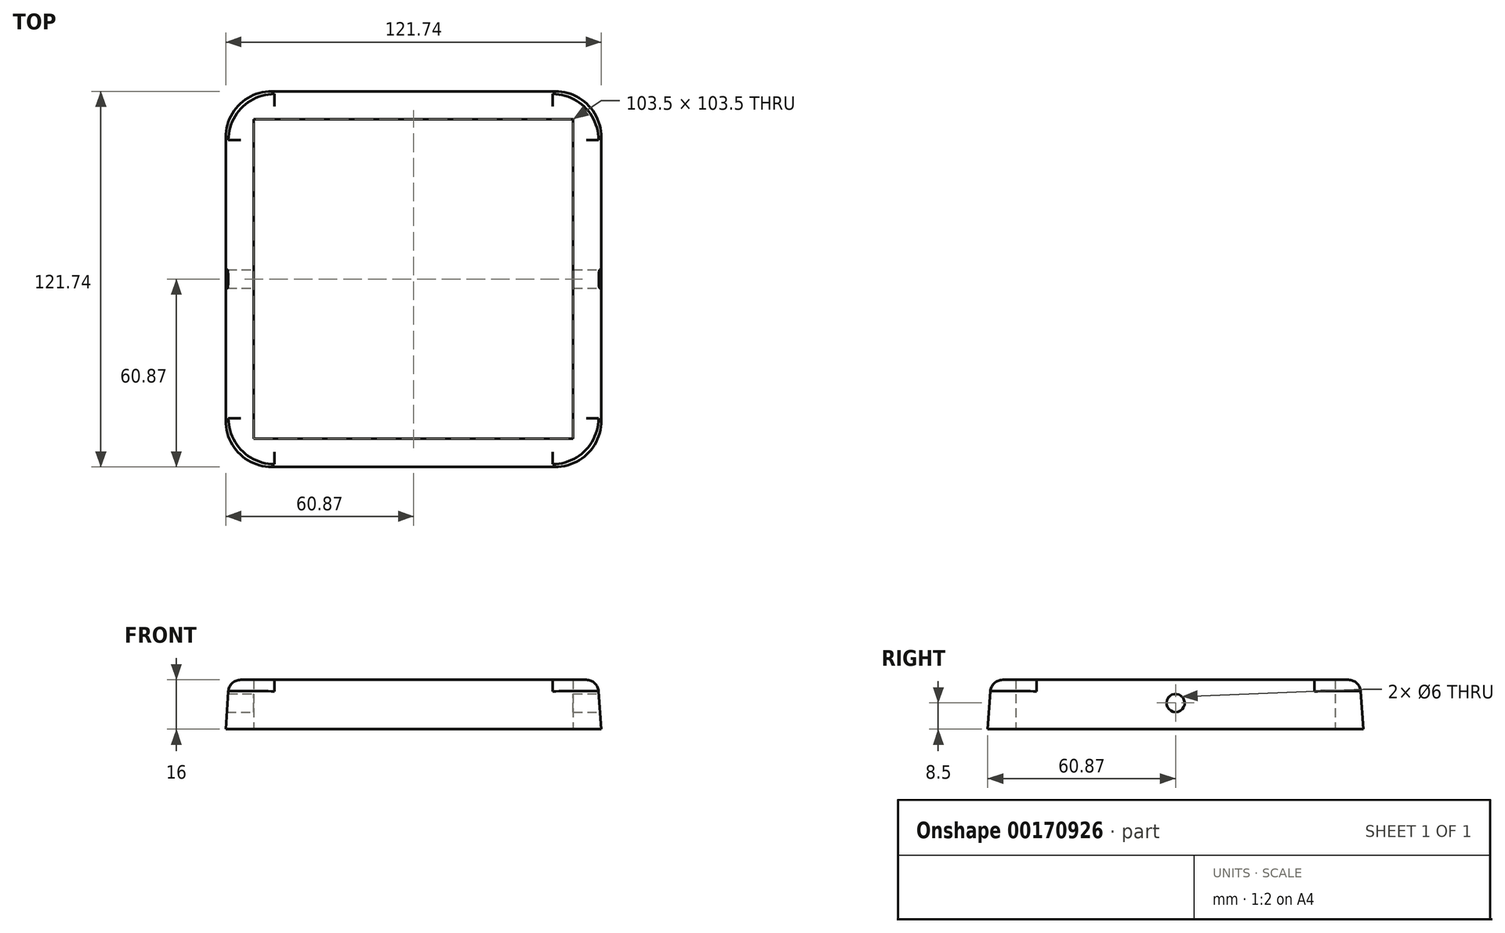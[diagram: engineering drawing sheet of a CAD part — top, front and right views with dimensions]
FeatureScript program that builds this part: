
annotation { "Feature Type Name" : "Feature", "Feature Type Description" : "" }
export const myFeature = defineFeature(function(context is Context, id is Id, definition is map)
    precondition{}
    {
        {
            var Q0;
            Q0=qCreatedBy(makeId("Top.planeOp"),FACE);
            var sketch = newSketch(context, id + "F0", { "sketchPlane" : qUnion([Q0])});
            skLineSegment(sketch, "E0.bottom", {"start": v(51.25, 51.25) * mm, "end": v(-51.25, 51.25) * mm});
            skLineSegment(sketch, "E0.top", {"start": v(51.25, -51.25) * mm, "end": v(-51.25, -51.25) * mm});
            skLineSegment(sketch, "E0.left", {"start": v(51.25, 51.25) * mm, "end": v(51.25, -51.25) * mm});
            skLineSegment(sketch, "E0.right", {"start": v(-51.25, 51.25) * mm, "end": v(-51.25, -51.25) * mm});
            skPoint(sketch, "E0.middle", {"position": v(0, 0) * mm});
            skSolve(sketch);
        }
        {
            var Q0;
            Q0=makeQuery(id+"F0.imprint","IMPRINT",FACE,{"disambiguationData":[TD([[makeQuery(id+"F0.imprint","IMPRINT",EDGE,{"derivedFrom":sQuery(id+"F0.wireOp",EDGE,"E0.bottom")}),1.0]])]});
            extrude(context, id + "F1", {"entities" : qUnion([Q0]), "depth" : 100 * mm});
        }
        {
            var Q0;
            Q0=makeQuery(id+"F1.opExtrude","CAP_FACE",FACE,{"disambiguationData":[OSD([sQuery(id+"F0.wireOp",EDGE,"E0.bottom"),sQuery(id+"F0.wireOp",EDGE,"E0.top"),sQuery(id+"F0.wireOp",EDGE,"E0.left"),sQuery(id+"F0.wireOp",EDGE,"E0.right")])],"isStart":false});
            var sketch = newSketch(context, id + "F2", { "sketchPlane" : qUnion([Q0])});
            skLineSegment(sketch, "E1.0", {"start": v(51.75, -51.75) * mm, "end": v(-51.75, -51.75) * mm});
            skLineSegment(sketch, "E1.1", {"start": v(51.75, 51.75) * mm, "end": v(51.75, -51.75) * mm});
            skLineSegment(sketch, "E1.2", {"start": v(51.75, 51.75) * mm, "end": v(-51.75, 51.75) * mm});
            skLineSegment(sketch, "E1.3", {"start": v(-51.75, 51.75) * mm, "end": v(-51.75, -51.75) * mm});
            skLineSegment(sketch, "E2.bottom", {"start": v(59.75, 59.75) * mm, "end": v(-59.75, 59.75) * mm});
            skLineSegment(sketch, "E2.top", {"start": v(59.75, -59.75) * mm, "end": v(-59.75, -59.75) * mm});
            skLineSegment(sketch, "E2.left", {"start": v(59.75, 59.75) * mm, "end": v(59.75, -59.75) * mm});
            skLineSegment(sketch, "E2.right", {"start": v(-59.75, 59.75) * mm, "end": v(-59.75, -59.75) * mm});
            skPoint(sketch, "E2.middle", {"position": v(0, 0) * mm});
            skSolve(sketch);
        }
        {
            var Q0;
            Q0 = qSketchRegion(id + "F2", true);
            extrude(context, id + "F3", {"entities" : qUnion([Q0]), "oppositeDirection" : true, "depth" : 16 * mm, "hasDraft" : true, "draftAngle" : 4 * degree});
        }
        {
            var Q0;
            Q0=makeQuery(id+"F3.opExtrude","SWEPT_EDGE",EDGE,{"disambiguationData":[OSD([sQuery(id+"F2.wireOp",EDGE,"E2.top"),sQuery(id+"F2.wireOp",EDGE,"E2.right")])]});
            var Q1;
            Q1=makeQuery(id+"F3.opExtrude","SWEPT_EDGE",EDGE,{"disambiguationData":[OSD([sQuery(id+"F2.wireOp",EDGE,"E2.bottom"),sQuery(id+"F2.wireOp",EDGE,"E2.right")])]});
            var Q2;
            Q2=makeQuery(id+"F3.opExtrude","SWEPT_EDGE",EDGE,{"disambiguationData":[OSD([sQuery(id+"F2.wireOp",EDGE,"E2.top"),sQuery(id+"F2.wireOp",EDGE,"E2.left")])]});
            var Q3;
            Q3=makeQuery(id+"F3.opExtrude","SWEPT_EDGE",EDGE,{"disambiguationData":[OSD([sQuery(id+"F2.wireOp",EDGE,"E2.bottom"),sQuery(id+"F2.wireOp",EDGE,"E2.left")])]});
            fillet(context, id + "F4", {"entities" : qUnion([Q0, Q1, Q2, Q3]), "radius" : 15 * mm, "tangentPropagation" : true, "allowEdgeOverflow" : false});
        }
        {
            var Q0;
            Q0=makeQuery(id+"F3.opExtrude","CAP_EDGE",EDGE,{"disambiguationData":[OSD([sQuery(id+"F2.wireOp",EDGE,"E2.top")])],"isStart":true});
            var Q1;
            {var subQ0=sQuery(id+"F2.wireOp",EDGE,"E2.right");var subQ1=sQuery(id+"F2.wireOp",EDGE,"E2.top");Q1=makeQuery(id+"F4.opFillet","BLEND_EDGE",EDGE,{"blendedFrom":[makeQuery(id+"F3.opExtrude","SWEPT_EDGE",EDGE,{"disambiguationData":[OSD([subQ1,subQ0])]}),makeQuery(id+"F3.opExtrude","CAP_FACE",FACE,{"disambiguationData":[OSD([sQuery(id+"F2.wireOp",EDGE,"E1.0"),sQuery(id+"F2.wireOp",EDGE,"E1.1"),sQuery(id+"F2.wireOp",EDGE,"E1.2"),sQuery(id+"F2.wireOp",EDGE,"E1.3"),sQuery(id+"F2.wireOp",EDGE,"E2.bottom"),subQ1,sQuery(id+"F2.wireOp",EDGE,"E2.left"),subQ0])],"isStart":true})],"blendedInto":[makeQuery(id+"F3.opExtrude","CAP_FACE",FACE,{"disambiguationData":[OSD([sQuery(id+"F2.wireOp",EDGE,"E1.0"),sQuery(id+"F2.wireOp",EDGE,"E1.1"),sQuery(id+"F2.wireOp",EDGE,"E1.2"),sQuery(id+"F2.wireOp",EDGE,"E1.3"),sQuery(id+"F2.wireOp",EDGE,"E2.bottom"),subQ1,sQuery(id+"F2.wireOp",EDGE,"E2.left"),subQ0])],"isStart":true})]});}
            fillet(context, id + "F5", {"entities" : qUnion([Q0, Q1]), "radius" : 4 * mm, "tangentPropagation" : true, "allowEdgeOverflow" : false});
        }
        {
            var Q0;
            Q0=qCreatedBy(makeId("Right.planeOp"),FACE);
            var sketch = newSketch(context, id + "F6", { "sketchPlane" : qUnion([Q0])});
            skCircle(sketch, "E3", {"center": v(0, 92.5) * mm, "radius": 3 * mm});
            skLineSegment(sketch, "E4.0", {"start": v(45.9, 84) * mm, "end": v(-45.9, 84) * mm, "construction": true});
            skSolve(sketch);
        }
        {
            var Q0;
            Q0 = qSketchRegion(id + "F6", true);
            extrude(context, id + "F7", {"entities" : qUnion([Q0]), "operationType" : NewBodyOperationType.REMOVE, "endBound" : BoundingType.SYMMETRIC, "oppositeDirection" : true, "depth" : 150 * mm});
        }
        {
            var Q0;
            Q0=qCreatedBy(makeId("Top.planeOp"),FACE);
            var sketch = newSketch(context, id + "F8", { "sketchPlane" : qUnion([Q0])});
            skLineSegment(sketch, "E5.bottom", {"start": v(51.75, 51.75) * mm, "end": v(-51.75, 51.75) * mm});
            skLineSegment(sketch, "E5.top", {"start": v(51.75, -51.75) * mm, "end": v(-51.75, -51.75) * mm});
            skLineSegment(sketch, "E5.left", {"start": v(51.75, 51.75) * mm, "end": v(51.75, -51.75) * mm});
            skLineSegment(sketch, "E5.right", {"start": v(-51.75, 51.75) * mm, "end": v(-51.75, -51.75) * mm});
            skPoint(sketch, "E5.middle", {"position": v(0, 0) * mm});
            skSolve(sketch);
        }
        {
            var Q0;
            Q0=makeQuery(id+"F8.imprint","IMPRINT",FACE,{"disambiguationData":[TD([[makeQuery(id+"F8.imprint","IMPRINT",EDGE,{"derivedFrom":sQuery(id+"F8.wireOp",EDGE,"E5.bottom")}),1.0]])]});
            extrude(context, id + "F9", {"entities" : qUnion([Q0]), "operationType" : NewBodyOperationType.REMOVE, "endBound" : BoundingType.THROUGH_ALL, "depth" : 25 * mm});
        }
    });
